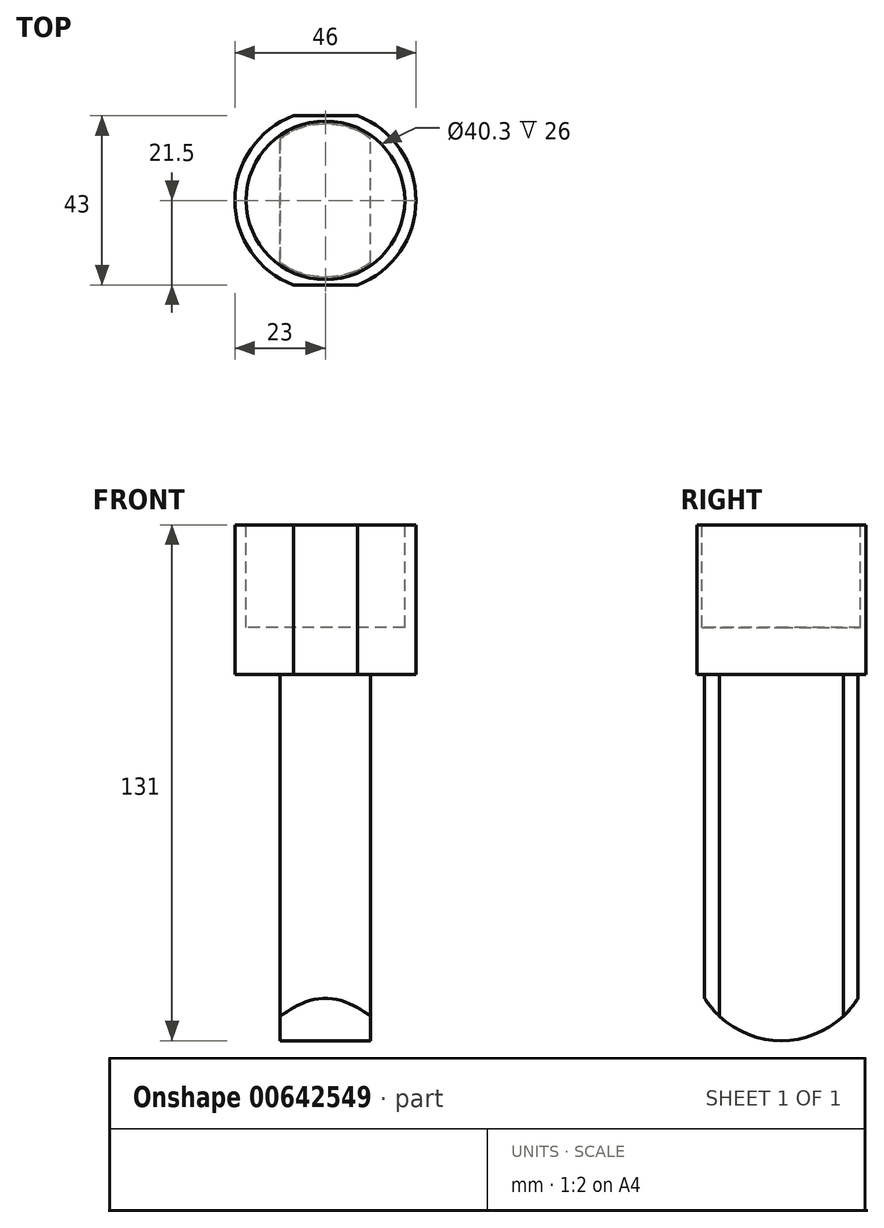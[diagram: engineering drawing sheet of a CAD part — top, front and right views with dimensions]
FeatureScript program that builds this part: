
annotation { "Feature Type Name" : "Feature", "Feature Type Description" : "" }
export const myFeature = defineFeature(function(context is Context, id is Id, definition is map)
    precondition{}
    {
        {
            var Q0;
            Q0=qCreatedBy(makeId("Top.planeOp"),FACE);
            var sketch = newSketch(context, id + "F0", { "sketchPlane" : qUnion([Q0])});
            skArc(sketch, "E0", {"start": v(-8.17, 21.5) * mm, "mid": v(-23, 0) * mm, "end": v(-8.17, -21.5) * mm});
            skLineSegment(sketch, "E1", {"start": v(-8.17, 21.5) * mm, "end": v(8.17, 21.5) * mm});
            skLineSegment(sketch, "E2.MirrorCS", {"start": v(-8.17, -21.5) * mm, "end": v(8.17, -21.5) * mm});
            skArc(sketch, "E3.trimOffspring", {"start": v(8.17, -21.5) * mm, "mid": v(23, 0) * mm, "end": v(8.17, 21.5) * mm});
            skSolve(sketch);
        }
        {
            var Q0;
            Q0 = qSketchRegion(id + "F0", true);
            extrude(context, id + "F1", {"entities" : qUnion([Q0]), "depth" : 38 * mm, "offsetDistance" : 25 * mm});
        }
        {
            var Q0;
            Q0=makeQuery(id+"F1.opExtrude","CAP_FACE",FACE,{"disambiguationData":[OSD([sQuery(id+"F0.wireOp",EDGE,"E0"),sQuery(id+"F0.wireOp",EDGE,"E1"),sQuery(id+"F0.wireOp",EDGE,"E2.MirrorCS"),sQuery(id+"F0.wireOp",EDGE,"E3.trimOffspring")])],"isStart":false});
            var sketch = newSketch(context, id + "F2", { "sketchPlane" : qUnion([Q0])});
            skCircle(sketch, "E4", {"center": v(0, 0) * mm, "radius": 20.15 * mm});
            skSolve(sketch);
        }
        {
            var Q0;
            Q0 = qSketchRegion(id + "F2", true);
            extrude(context, id + "F3", {"entities" : qUnion([Q0]), "operationType" : NewBodyOperationType.REMOVE, "oppositeDirection" : true, "depth" : 26 * mm, "offsetDistance" : 25 * mm});
        }
        {
            var Q0;
            Q0=makeQuery(id+"F1.opExtrude","CAP_FACE",FACE,{"disambiguationData":[OSD([sQuery(id+"F0.wireOp",EDGE,"E0"),sQuery(id+"F0.wireOp",EDGE,"E1"),sQuery(id+"F0.wireOp",EDGE,"E2.MirrorCS"),sQuery(id+"F0.wireOp",EDGE,"E3.trimOffspring")])],"isStart":true});
            var sketch = newSketch(context, id + "F4", { "sketchPlane" : qUnion([Q0])});
            skArc(sketch, "E5", {"start": v(-11.5, -15.75) * mm, "mid": v(0, -19.5) * mm, "end": v(11.5, -15.75) * mm});
            skLineSegment(sketch, "E6", {"start": v(-11.5, 15.75) * mm, "end": v(-11.5, -15.75) * mm});
            skLineSegment(sketch, "E7.MirrorCS", {"start": v(11.5, 15.75) * mm, "end": v(11.5, -15.75) * mm});
            skArc(sketch, "E8.trimOffspring", {"start": v(11.5, 15.75) * mm, "mid": v(0, 19.5) * mm, "end": v(-11.5, 15.75) * mm});
            skSolve(sketch);
        }
        {
            var Q0;
            Q0=makeQuery(id+"F4.imprint","IMPRINT",FACE,{"disambiguationData":[TD([[makeQuery(id+"F4.imprint","IMPRINT",EDGE,{"derivedFrom":sQuery(id+"F4.wireOp",EDGE,"E5")}),1.0]])]});
            extrude(context, id + "F5", {"entities" : qUnion([Q0]), "operationType" : NewBodyOperationType.ADD, "depth" : 93 * mm, "offsetDistance" : 25 * mm});
        }
        {
            var Q0;
            Q0=makeQuery(id+"F5.opExtrude","SWEPT_FACE",FACE,{"disambiguationData":[OSD([sQuery(id+"F4.wireOp",EDGE,"E6")])]});
            var sketch = newSketch(context, id + "F6", { "sketchPlane" : qUnion([Q0])});
            skArc(sketch, "E9", {"start": v(-23, -70.03) * mm, "mid": v(0, -93) * mm, "end": v(23, -70.03) * mm});
            skLineSegment(sketch, "E10", {"start": v(-23, -70.03) * mm, "end": v(23, -70.03) * mm});
            skLineSegment(sketch, "E11", {"start": v(23, -70.03) * mm, "end": v(40.12, -102.5) * mm});
            skLineSegment(sketch, "E12", {"start": v(40.12, -102.5) * mm, "end": v(-43.34, -102.5) * mm});
            skLineSegment(sketch, "E13", {"start": v(-43.34, -102.5) * mm, "end": v(-23, -70.03) * mm});
            skSolve(sketch);
        }
        {
            var Q0;
            {var subQ0=sQuery(id+"F6.wireOp",EDGE,"E11");Q0=makeQuery(id+"F6.imprint","IMPRINT",FACE,{"disambiguationData":[TD([[makeQuery(id+"F6.imprint","IMPRINT",EDGE,{"derivedFrom":subQ0}),-1.0]])]});}
            var Q1;
            {var subQ0=sQuery(id+"F6.wireOp",EDGE,"E9");var subQ1=sQuery(id+"F4.wireOp",EDGE,"E6");var subQ2=makeQuery(id+"F5.opExtrude","CAP_EDGE",EDGE,{"disambiguationData":[OSD([subQ1])],"isStart":false});var subQ3=makeQuery(id+"F6.imprint","INTERSECT",VERTEX,{"derivedFrom":[subQ2,subQ0]});Q1=makeQuery(id+"F6.imprint","IMPRINT",FACE,{"disambiguationData":[TD([[makeQuery(id+"F6.imprint","IMPRINT",EDGE,{"disambiguationData":[TD([[subQ3,-1.0]])],"derivedFrom":subQ0}),-1.0]])]});}
            var Q2;
            {var subQ0=sQuery(id+"F6.wireOp",EDGE,"E9");var subQ1=sQuery(id+"F4.wireOp",EDGE,"E6");var subQ4=makeQuery(id+"F5.opExtrude","CAP_EDGE",EDGE,{"disambiguationData":[OSD([subQ1])],"isStart":false});var subQ5=makeQuery(id+"F6.imprint","INTERSECT",VERTEX,{"derivedFrom":[subQ4,subQ0]});Q2=makeQuery(id+"F6.imprint","IMPRINT",FACE,{"disambiguationData":[TD([[makeQuery(id+"F6.imprint","IMPRINT",EDGE,{"disambiguationData":[TD([[subQ5,1.0]])],"derivedFrom":subQ0}),-1.0]])]});}
            extrude(context, id + "F7", {"entities" : qUnion([Q0, Q1, Q2]), "operationType" : NewBodyOperationType.REMOVE, "oppositeDirection" : true, "depth" : 25 * mm, "offsetDistance" : 25 * mm});
        }
    });
